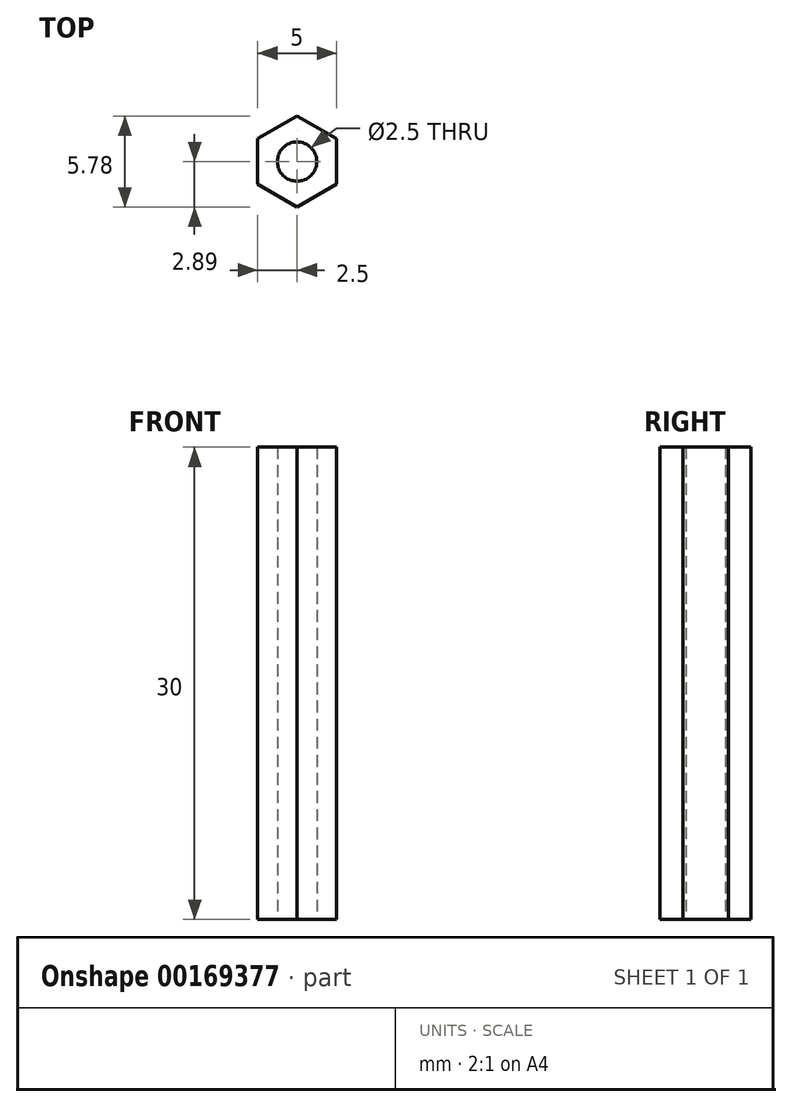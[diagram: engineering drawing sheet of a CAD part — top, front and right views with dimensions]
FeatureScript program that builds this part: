
annotation { "Feature Type Name" : "Feature", "Feature Type Description" : "" }
export const myFeature = defineFeature(function(context is Context, id is Id, definition is map)
    precondition{}
    {
        {
            var Q0;
            Q0=qCreatedBy(makeId("Top.planeOp"),FACE);
            var sketch = newSketch(context, id + "F0", { "sketchPlane" : qUnion([Q0])});
            skCircle(sketch, "E0", {"center": v(0, 0) * mm, "radius": 1.25 * mm});
            skCircle(sketch, "E1.cCircle", {"center": v(0, 0) * mm, "radius": 2.5 * mm, "construction": true});
            skLineSegment(sketch, "E1.0", {"start": v(-2.5, -1.44) * mm, "end": v(-2.5, 1.44) * mm});
            skLineSegment(sketch, "E1.1", {"start": v(-2.5, 1.44) * mm, "end": v(0, 2.89) * mm});
            skLineSegment(sketch, "E1.2", {"start": v(0, 2.89) * mm, "end": v(2.5, 1.44) * mm});
            skLineSegment(sketch, "E1.3", {"start": v(2.5, 1.44) * mm, "end": v(2.5, -1.44) * mm});
            skLineSegment(sketch, "E1.4", {"start": v(2.5, -1.44) * mm, "end": v(0, -2.89) * mm});
            skLineSegment(sketch, "E1.5", {"start": v(0, -2.89) * mm, "end": v(-2.5, -1.44) * mm});
            skPoint(sketch, "E1.0.midPoint", {"position": v(-2.5, 0) * mm});
            skSolve(sketch);
        }
        {
            var Q0;
            Q0 = qSketchRegion(id + "F0", true);
            extrude(context, id + "F1", {"entities" : qUnion([Q0]), "depth" : 30 * mm});
        }
    });
